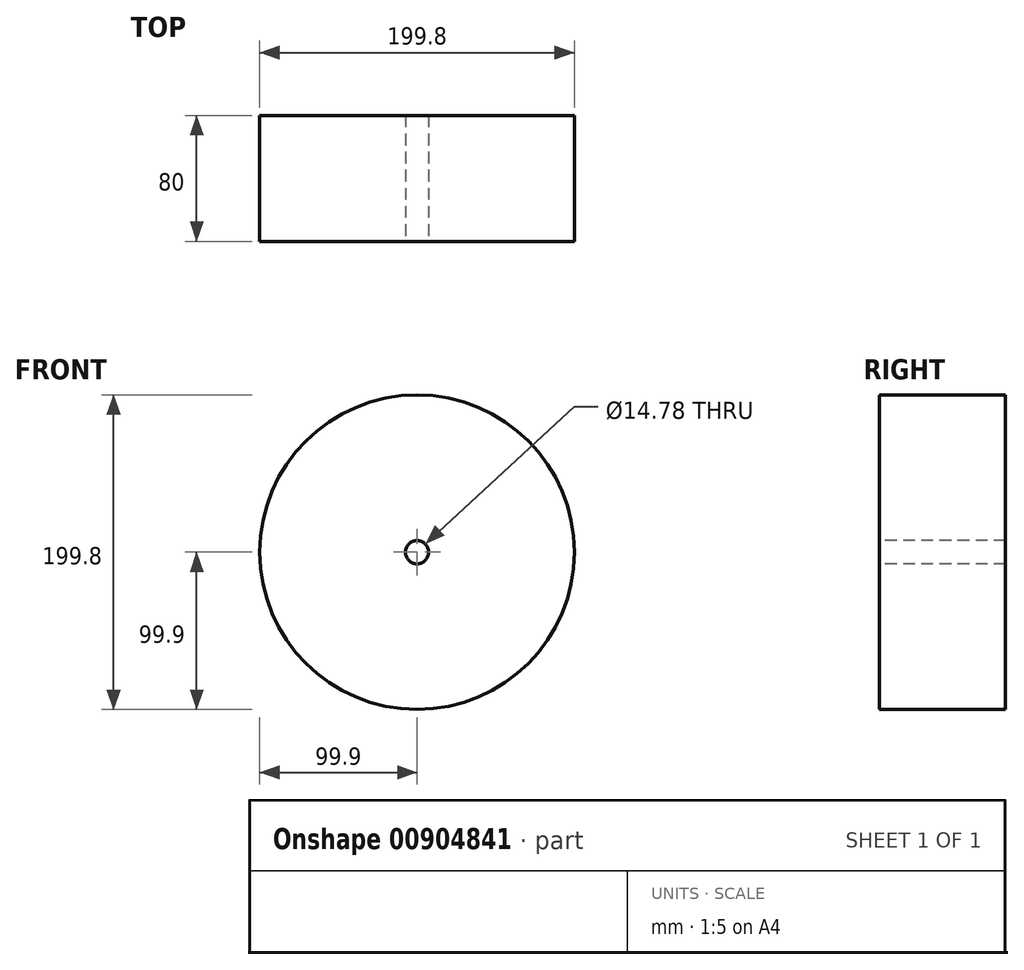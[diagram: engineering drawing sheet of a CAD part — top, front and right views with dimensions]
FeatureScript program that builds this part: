
annotation { "Feature Type Name" : "Feature", "Feature Type Description" : "" }
export const myFeature = defineFeature(function(context is Context, id is Id, definition is map)
    precondition{}
    {
        {
            var Q0;
            Q0=qCreatedBy(makeId("Front.planeOp"),FACE);
            var sketch = newSketch(context, id + "F0", { "sketchPlane" : qUnion([Q0])});
            skCircle(sketch, "E0", {"center": v(0, 0) * mm, "radius": 99.9 * mm});
            skSolve(sketch);
        }
        {
            var Q0;
            Q0=makeQuery(id+"F0.imprint","IMPRINT",FACE,{"disambiguationData":[TD([[makeQuery(id+"F0.imprint","IMPRINT",EDGE,{"derivedFrom":sQuery(id+"F0.wireOp",EDGE,"E0")}),1.0]])]});
            extrude(context, id + "F1", {"entities" : qUnion([Q0]), "depth" : 50 * mm, "offsetDistance" : 25 * mm});
        }
        {
            var Q0;
            Q0=makeQuery(id+"F1.opExtrude","CAP_FACE",FACE,{"disambiguationData":[OSD([sQuery(id+"F0.wireOp",EDGE,"E0")])],"isStart":false});
            var sketch = newSketch(context, id + "F2", { "sketchPlane" : qUnion([Q0])});
            skPoint(sketch, "E1", {"position": v(0, 0) * mm});
            skCircle(sketch, "E2", {"center": v(0, 0) * mm, "radius": 7.39 * mm});
            skSolve(sketch);
        }
        {
            var Q0;
            Q0=makeQuery(id+"F2.imprint","IMPRINT",FACE,{"disambiguationData":[TD([[makeQuery(id+"F2.imprint","IMPRINT",EDGE,{"derivedFrom":sQuery(id+"F2.wireOp",EDGE,"E2")}),1.0]])]});
            extrude(context, id + "F3", {"entities" : qUnion([Q0]), "operationType" : NewBodyOperationType.REMOVE, "endBound" : BoundingType.THROUGH_ALL, "oppositeDirection" : true, "depth" : 25 * mm, "offsetDistance" : 25 * mm});
        }
        {
            var Q0;
            Q0=makeQuery(id+"F1.opExtrude","CAP_FACE",FACE,{"disambiguationData":[OSD([sQuery(id+"F0.wireOp",EDGE,"E0")])],"isStart":false});
            extrude(context, id + "F4", {"entities" : qUnion([Q0]), "operationType" : NewBodyOperationType.ADD, "depth" : 50 * mm, "offsetDistance" : 25 * mm});
        }
        {
            var Q0;
            Q0=makeQuery(id+"F4.opExtrude","CAP_FACE",FACE,{"disambiguationData":[OSD([sQuery(id+"F0.wireOp",EDGE,"E0")])],"isStart":false});
            extrude(context, id + "F5", {"entities" : qUnion([Q0]), "operationType" : NewBodyOperationType.REMOVE, "oppositeDirection" : true, "depth" : 20 * mm, "offsetDistance" : 25 * mm});
        }
    });
